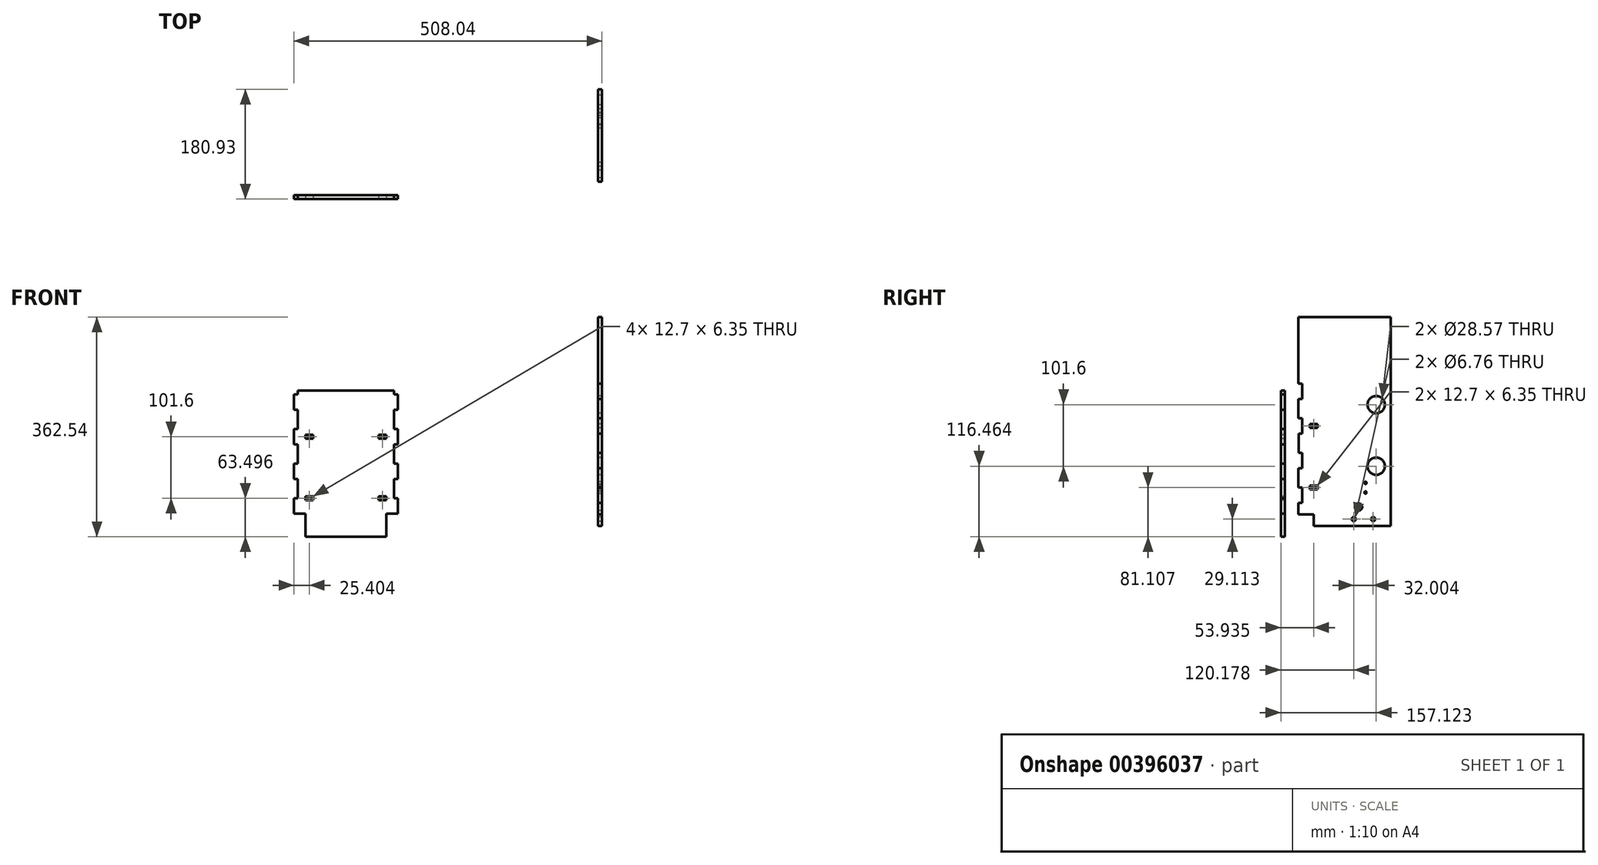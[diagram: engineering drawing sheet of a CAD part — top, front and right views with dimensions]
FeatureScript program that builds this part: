
annotation { "Feature Type Name" : "Feature", "Feature Type Description" : "" }
export const myFeature = defineFeature(function(context is Context, id is Id, definition is map)
    precondition{}
    {
        {
            var Q0;
            Q0=qCreatedBy(makeId("Front.planeOp"),FACE);
            var sketch = newSketch(context, id + "F0", { "sketchPlane" : qUnion([Q0])});
            skLineSegment(sketch, "E0.top", {"start": v(-501.69, -243.4) * mm, "end": v(-330.24, -243.4) * mm});
            skLineSegment(sketch, "E1", {"start": v(-495.34, -2.1) * mm, "end": v(-495.34, -243.4) * mm});
            skLineSegment(sketch, "E2", {"start": v(-501.69, -8.44) * mm, "end": v(-495.34, -8.44) * mm});
            skLineSegment(sketch, "E3", {"start": v(-501.69, -33.84) * mm, "end": v(-495.34, -33.84) * mm});
            skLineSegment(sketch, "E4", {"start": v(-501.69, -65.6) * mm, "end": v(-495.34, -65.6) * mm});
            skLineSegment(sketch, "E5", {"start": v(-501.69, -91) * mm, "end": v(-495.34, -91) * mm});
            skLineSegment(sketch, "E6", {"start": v(-501.69, -122.74) * mm, "end": v(-495.34, -122.74) * mm});
            skLineSegment(sketch, "E7", {"start": v(-501.69, -148.14) * mm, "end": v(-495.34, -148.14) * mm});
            skLineSegment(sketch, "E8", {"start": v(-501.69, -179.9) * mm, "end": v(-495.34, -179.9) * mm});
            skLineSegment(sketch, "E9", {"start": v(-501.69, -205.3) * mm, "end": v(-495.34, -205.3) * mm});
            skLineSegment(sketch, "E10", {"start": v(-501.69, -237.04) * mm, "end": v(-495.34, -237.04) * mm});
            skLineSegment(sketch, "E11", {"start": v(-501.69, -8.44) * mm, "end": v(-501.69, -33.84) * mm});
            skLineSegment(sketch, "E12", {"start": v(-501.69, -65.6) * mm, "end": v(-501.69, -91) * mm});
            skLineSegment(sketch, "E13", {"start": v(-501.69, -122.74) * mm, "end": v(-501.69, -148.14) * mm});
            skLineSegment(sketch, "E14", {"start": v(-501.69, -179.9) * mm, "end": v(-501.69, -205.3) * mm});
            skLineSegment(sketch, "E15", {"start": v(-501.69, -237.04) * mm, "end": v(-501.69, -243.4) * mm});
            skLineSegment(sketch, "E16", {"start": v(-336.59, -2.1) * mm, "end": v(-336.59, -243.4) * mm});
            skLineSegment(sketch, "E17", {"start": v(-336.59, -8.44) * mm, "end": v(-330.24, -8.44) * mm});
            skLineSegment(sketch, "E18", {"start": v(-336.59, -33.84) * mm, "end": v(-330.24, -33.84) * mm});
            skLineSegment(sketch, "E19", {"start": v(-336.59, -65.6) * mm, "end": v(-330.24, -65.6) * mm});
            skLineSegment(sketch, "E20", {"start": v(-336.59, -91) * mm, "end": v(-330.24, -91) * mm});
            skLineSegment(sketch, "E21", {"start": v(-336.59, -122.74) * mm, "end": v(-330.24, -122.74) * mm});
            skLineSegment(sketch, "E22", {"start": v(-336.59, -148.14) * mm, "end": v(-330.24, -148.14) * mm});
            skLineSegment(sketch, "E23", {"start": v(-336.59, -179.9) * mm, "end": v(-330.24, -179.9) * mm});
            skLineSegment(sketch, "E24", {"start": v(-336.59, -205.3) * mm, "end": v(-330.24, -205.3) * mm});
            skLineSegment(sketch, "E25", {"start": v(-336.59, -237.04) * mm, "end": v(-330.24, -237.04) * mm});
            skLineSegment(sketch, "E26", {"start": v(-330.24, -8.44) * mm, "end": v(-330.24, -33.84) * mm});
            skLineSegment(sketch, "E27", {"start": v(-330.24, -65.6) * mm, "end": v(-330.24, -91) * mm});
            skLineSegment(sketch, "E28", {"start": v(-330.24, -122.74) * mm, "end": v(-330.24, -148.14) * mm});
            skLineSegment(sketch, "E29", {"start": v(-330.24, -179.9) * mm, "end": v(-330.24, -205.3) * mm});
            skLineSegment(sketch, "E30", {"start": v(-330.24, -237.04) * mm, "end": v(-330.24, -243.4) * mm});
            skLineSegment(sketch, "E31", {"start": v(-495.34, -2.1) * mm, "end": v(-336.59, -2.1) * mm});
            skSolve(sketch);
        }
        {
            var Q0;
            {var subQ5=sQuery(id+"F0.wireOp",EDGE,"E0.bottom");var subQ8=sQuery(id+"F0.wireOp",EDGE,"E1");var subQ20=makeQuery(id+"F0.imprint","INTERSECT",VERTEX,{"derivedFrom":[subQ5,subQ8]});Q0=makeQuery(id+"F0.imprint","IMPRINT",FACE,{"disambiguationData":[TD([[makeQuery(id+"F0.imprint","IMPRINT",EDGE,{"disambiguationData":[TD([[subQ20,-1.0]])],"derivedFrom":subQ5}),-1.0]])]});}
            var Q1;
            {var subQ4=sQuery(id+"F0.wireOp",EDGE,"LMsAul2w-vVBP-qz1e-n2hl-ZY3DGVZ1hmQM");Q1=makeQuery(id+"F0.imprint","IMPRINT",FACE,{"disambiguationData":[TD([[makeQuery(id+"F0.imprint","IMPRINT",EDGE,{"derivedFrom":subQ4}),1.0]])]});}
            var Q2;
            {var subQ0=sQuery(id+"F0.wireOp",EDGE,"E2");Q2=makeQuery(id+"F0.imprint","IMPRINT",FACE,{"disambiguationData":[TD([[makeQuery(id+"F0.imprint","IMPRINT",EDGE,{"derivedFrom":subQ0}),-1.0]])]});}
            var Q3;
            {var subQ0=sQuery(id+"F0.wireOp",EDGE,"E4");Q3=makeQuery(id+"F0.imprint","IMPRINT",FACE,{"disambiguationData":[TD([[makeQuery(id+"F0.imprint","IMPRINT",EDGE,{"derivedFrom":subQ0}),-1.0]])]});}
            var Q4;
            {var subQ0=sQuery(id+"F0.wireOp",EDGE,"E6");Q4=makeQuery(id+"F0.imprint","IMPRINT",FACE,{"disambiguationData":[TD([[makeQuery(id+"F0.imprint","IMPRINT",EDGE,{"derivedFrom":subQ0}),-1.0]])]});}
            var Q5;
            {var subQ0=sQuery(id+"F0.wireOp",EDGE,"E8");Q5=makeQuery(id+"F0.imprint","IMPRINT",FACE,{"disambiguationData":[TD([[makeQuery(id+"F0.imprint","IMPRINT",EDGE,{"derivedFrom":subQ0}),-1.0]])]});}
            var Q6;
            {var subQ4=sQuery(id+"F0.wireOp",EDGE,"E10");Q6=makeQuery(id+"F0.imprint","IMPRINT",FACE,{"disambiguationData":[TD([[makeQuery(id+"F0.imprint","IMPRINT",EDGE,{"derivedFrom":subQ4}),-1.0]])]});}
            var Q7;
            {var subQ4=sQuery(id+"F0.wireOp",EDGE,"E25");Q7=makeQuery(id+"F0.imprint","IMPRINT",FACE,{"disambiguationData":[TD([[makeQuery(id+"F0.imprint","IMPRINT",EDGE,{"derivedFrom":subQ4}),-1.0]])]});}
            var Q8;
            {var subQ0=sQuery(id+"F0.wireOp",EDGE,"E23");Q8=makeQuery(id+"F0.imprint","IMPRINT",FACE,{"disambiguationData":[TD([[makeQuery(id+"F0.imprint","IMPRINT",EDGE,{"derivedFrom":subQ0}),-1.0]])]});}
            var Q9;
            {var subQ0=sQuery(id+"F0.wireOp",EDGE,"E21");Q9=makeQuery(id+"F0.imprint","IMPRINT",FACE,{"disambiguationData":[TD([[makeQuery(id+"F0.imprint","IMPRINT",EDGE,{"derivedFrom":subQ0}),-1.0]])]});}
            var Q10;
            {var subQ0=sQuery(id+"F0.wireOp",EDGE,"E19");Q10=makeQuery(id+"F0.imprint","IMPRINT",FACE,{"disambiguationData":[TD([[makeQuery(id+"F0.imprint","IMPRINT",EDGE,{"derivedFrom":subQ0}),-1.0]])]});}
            var Q11;
            {var subQ0=sQuery(id+"F0.wireOp",EDGE,"E17");Q11=makeQuery(id+"F0.imprint","IMPRINT",FACE,{"disambiguationData":[TD([[makeQuery(id+"F0.imprint","IMPRINT",EDGE,{"derivedFrom":subQ0}),-1.0]])]});}
            var Q12;
            {var subQ4=sQuery(id+"F0.wireOp",EDGE,"Q2wxjBHx-EqrT-55AE-FTu7-pREpD65ahsZC");Q12=makeQuery(id+"F0.imprint","IMPRINT",FACE,{"disambiguationData":[TD([[makeQuery(id+"F0.imprint","IMPRINT",EDGE,{"derivedFrom":subQ4}),1.0]])]});}
            var Q13;
            {var subQ12=sQuery(id+"F0.wireOp",EDGE,"E31");Q13=makeQuery(id+"F0.imprint","IMPRINT",FACE,{"disambiguationData":[TD([[makeQuery(id+"F0.imprint","IMPRINT",EDGE,{"derivedFrom":subQ12}),-1.0]])]});}
            extrude(context, id + "F1", {"entities" : qUnion([Q0, Q1, Q2, Q3, Q4, Q5, Q6, Q7, Q8, Q9, Q10, Q11, Q12, Q13]), "depth" : 6.35 * mm});
        }
        {
            var Q0;
            Q0=qCreatedBy(makeId("Right.planeOp"),FACE);
            var sketch = newSketch(context, id + "F2", { "sketchPlane" : qUnion([Q0])});
            skLineSegment(sketch, "E32", {"start": v(28.53, -16.23) * mm, "end": v(22.18, -16.23) * mm});
            skLineSegment(sketch, "E33", {"start": v(28.53, -130.53) * mm, "end": v(22.18, -130.53) * mm});
            skLineSegment(sketch, "E34", {"start": v(28.53, -162.28) * mm, "end": v(22.18, -162.28) * mm});
            skLineSegment(sketch, "E35", {"start": v(28.53, -187.68) * mm, "end": v(22.18, -187.68) * mm});
            skLineSegment(sketch, "E36", {"start": v(28.53, -225.78) * mm, "end": v(22.18, -225.78) * mm});
            skLineSegment(sketch, "E37", {"start": v(28.53, -73.38) * mm, "end": v(22.8, -73.38) * mm});
            skLineSegment(sketch, "E38", {"start": v(28.53, -105.13) * mm, "end": v(22.8, -105.13) * mm});
            skLineSegment(sketch, "E39", {"start": v(22.8, -73.38) * mm, "end": v(22.8, -105.13) * mm});
            skLineSegment(sketch, "E40", {"start": v(22.18, -16.23) * mm, "end": v(22.18, -47.98) * mm});
            skLineSegment(sketch, "E41", {"start": v(22.18, -130.53) * mm, "end": v(22.18, -162.28) * mm});
            skLineSegment(sketch, "E42", {"start": v(22.18, -187.68) * mm, "end": v(22.18, -225.78) * mm});
            skLineSegment(sketch, "E43", {"start": v(174.58, -251.18) * mm, "end": v(28.53, -251.18) * mm});
            skLineSegment(sketch, "E44", {"start": v(22.18, 119.15) * mm, "end": v(174.58, 119.15) * mm});
            skLineSegment(sketch, "E45", {"start": v(174.58, 119.15) * mm, "end": v(174.58, -251.18) * mm});
            skLineSegment(sketch, "E46", {"start": v(28.53, -251.18) * mm, "end": v(28.53, 119.15) * mm});
            skLineSegment(sketch, "E47", {"start": v(22.18, -47.98) * mm, "end": v(28.53, -47.98) * mm});
            skLineSegment(sketch, "E48", {"start": v(28.53, 15.52) * mm, "end": v(22.18, 15.52) * mm});
            skLineSegment(sketch, "E49", {"start": v(22.18, 15.52) * mm, "end": v(22.18, 9.17) * mm});
            skLineSegment(sketch, "E50", {"start": v(22.18, 9.17) * mm, "end": v(28.53, 9.17) * mm});
            skLineSegment(sketch, "E51", {"start": v(22.18, 119.15) * mm, "end": v(22.18, 15.52) * mm});
            skLineSegment(sketch, "E52", {"start": v(28.53, -225.78) * mm, "end": v(174.58, -225.78) * mm});
            skLineSegment(sketch, "E53", {"start": v(22.18, -206.73) * mm, "end": v(47.58, -206.73) * mm});
            skLineSegment(sketch, "E54", {"start": v(47.58, -206.73) * mm, "end": v(47.58, -225.78) * mm});
            skSolve(sketch);
        }
        {
            var Q0;
            {var subQ14=sQuery(id+"F2.wireOp",EDGE,"i33fb0zR-01mT-Uh86-wEM1-dtgX8HlX7Fyt");Q0=makeQuery(id+"F2.imprint","IMPRINT",FACE,{"disambiguationData":[TD([[makeQuery(id+"F2.imprint","IMPRINT",EDGE,{"derivedFrom":subQ14}),1.0]])]});}
            var Q1;
            {var subQ4=sQuery(id+"F2.wireOp",EDGE,"rhUE6cCd-mflr-hycs-3UUx-SssaEqSjHUIw");Q1=makeQuery(id+"F2.imprint","IMPRINT",FACE,{"disambiguationData":[TD([[makeQuery(id+"F2.imprint","IMPRINT",EDGE,{"derivedFrom":subQ4}),-1.0]])]});}
            var Q2;
            {var subQ0=sQuery(id+"F2.wireOp",EDGE,"1oS58uJ2-hXIY-gExO-wKBo-R9qEpw5Eswbh");Q2=makeQuery(id+"F2.imprint","IMPRINT",FACE,{"disambiguationData":[TD([[makeQuery(id+"F2.imprint","IMPRINT",EDGE,{"derivedFrom":subQ0}),1.0]])]});}
            var Q3;
            {var subQ0=sQuery(id+"F2.wireOp",EDGE,"HLNgD7Xm-XkV7-PYZ1-Vyr9-8PbT4umlXNnn");Q3=makeQuery(id+"F2.imprint","IMPRINT",FACE,{"disambiguationData":[TD([[makeQuery(id+"F2.imprint","IMPRINT",EDGE,{"derivedFrom":subQ0}),1.0]])]});}
            var Q4;
            {var subQ0=sQuery(id+"F2.wireOp",EDGE,"S2SFkNX2-MHnE-1LtQ-Wrl6-HN21gxM6cwIg.top");Q4=makeQuery(id+"F2.imprint","IMPRINT",FACE,{"disambiguationData":[TD([[makeQuery(id+"F2.imprint","IMPRINT",EDGE,{"derivedFrom":subQ0}),1.0]])]});}
            var Q5;
            {var subQ0=sQuery(id+"F2.wireOp",EDGE,"nHbaO1BD-I0WF-YKfL-4D9o-AtkHzTHVU68h");Q5=makeQuery(id+"F2.imprint","IMPRINT",FACE,{"disambiguationData":[TD([[makeQuery(id+"F2.imprint","IMPRINT",EDGE,{"derivedFrom":subQ0}),1.0]])]});}
            var Q6;
            {var subQ0=sQuery(id+"F2.wireOp",EDGE,"e9KHasA0-oYsS-l2PR-DguL-FNIX4GsAtZwv");Q6=makeQuery(id+"F2.imprint","IMPRINT",FACE,{"disambiguationData":[TD([[makeQuery(id+"F2.imprint","IMPRINT",EDGE,{"derivedFrom":subQ0}),1.0]])]});}
            var Q7;
            {var subQ0=sQuery(id+"F2.wireOp",EDGE,"E37");Q7=makeQuery(id+"F2.imprint","IMPRINT",FACE,{"disambiguationData":[TD([[makeQuery(id+"F2.imprint","IMPRINT",EDGE,{"derivedFrom":subQ0}),1.0]])]});}
            var Q8;
            {var subQ0=sQuery(id+"F2.wireOp",EDGE,"E32");Q8=makeQuery(id+"F2.imprint","IMPRINT",FACE,{"disambiguationData":[TD([[makeQuery(id+"F2.imprint","IMPRINT",EDGE,{"derivedFrom":subQ0}),1.0]])]});}
            var Q9;
            {var subQ0=sQuery(id+"F2.wireOp",EDGE,"gp76ZxvM-iRQH-n3sY-OGDD-mYjBX4D9k2O5");Q9=makeQuery(id+"F2.imprint","IMPRINT",FACE,{"disambiguationData":[TD([[makeQuery(id+"F2.imprint","IMPRINT",EDGE,{"derivedFrom":subQ0}),1.0]])]});}
            var Q10;
            {var subQ0=sQuery(id+"F2.wireOp",EDGE,"E33");Q10=makeQuery(id+"F2.imprint","IMPRINT",FACE,{"disambiguationData":[TD([[makeQuery(id+"F2.imprint","IMPRINT",EDGE,{"derivedFrom":subQ0}),1.0]])]});}
            var Q11;
            {var subQ0=sQuery(id+"F2.wireOp",EDGE,"E35");Q11=makeQuery(id+"F2.imprint","IMPRINT",FACE,{"disambiguationData":[TD([[makeQuery(id+"F2.imprint","IMPRINT",EDGE,{"derivedFrom":subQ0}),1.0]])]});}
            var Q12;
            {var subQ4=sQuery(id+"F2.wireOp",EDGE,"E48");Q12=makeQuery(id+"F2.imprint","IMPRINT",FACE,{"disambiguationData":[TD([[makeQuery(id+"F2.imprint","IMPRINT",EDGE,{"derivedFrom":subQ4}),-1.0]])]});}
            var Q13;
            {var subQ0=sQuery(id+"F2.wireOp",EDGE,"E48");Q13=makeQuery(id+"F2.imprint","IMPRINT",FACE,{"disambiguationData":[TD([[makeQuery(id+"F2.imprint","IMPRINT",EDGE,{"derivedFrom":subQ0}),1.0]])]});}
            var Q14;
            {var subQ6=sQuery(id+"F2.wireOp",EDGE,"E54");Q14=makeQuery(id+"F2.imprint","IMPRINT",FACE,{"disambiguationData":[TD([[makeQuery(id+"F2.imprint","IMPRINT",EDGE,{"derivedFrom":subQ6}),1.0]])]});}
            extrude(context, id + "F3", {"entities" : qUnion([Q0, Q1, Q2, Q3, Q4, Q5, Q6, Q7, Q8, Q9, Q10, Q11, Q12, Q13, Q14]), "depth" : 6.35 * mm});
        }
        {
            var Q0;
            Q0=makeQuery(id+"F3.opExtrude","CAP_FACE",FACE,{"disambiguationData":[OSD([sQuery(id+"F2.wireOp",EDGE,"s0DKLVIk-yI4o-mbJo-Qtl3-NwG1ndSy3CrT"),sQuery(id+"F2.wireOp",EDGE,"E32"),sQuery(id+"F2.wireOp",EDGE,"bUhOaF83-sfzh-5jzX-XBu8-1UuN6AYuXBg6"),sQuery(id+"F2.wireOp",EDGE,"gp76ZxvM-iRQH-n3sY-OGDD-mYjBX4D9k2O5"),sQuery(id+"F2.wireOp",EDGE,"5Qirrqq4-OgZc-HNT0-THzN-mm1dnDsTKt5a"),sQuery(id+"F2.wireOp",EDGE,"E33"),sQuery(id+"F2.wireOp",EDGE,"E34"),sQuery(id+"F2.wireOp",EDGE,"E35"),sQuery(id+"F2.wireOp",EDGE,"E36"),sQuery(id+"F2.wireOp",EDGE,"rhUE6cCd-mflr-hycs-3UUx-SssaEqSjHUIw"),sQuery(id+"F2.wireOp",EDGE,"E37"),sQuery(id+"F2.wireOp",EDGE,"E38"),sQuery(id+"F2.wireOp",EDGE,"XDC90Sgm-SAT4-zVe1-7gUu-QymedyxHn4AY"),sQuery(id+"F2.wireOp",EDGE,"E39"),sQuery(id+"F2.wireOp",EDGE,"E40"),sQuery(id+"F2.wireOp",EDGE,"Gb2Q8Irj-KXKR-EalS-J060-aK0soJo5RwYU"),sQuery(id+"F2.wireOp",EDGE,"E41"),sQuery(id+"F2.wireOp",EDGE,"E42"),sQuery(id+"F2.wireOp",EDGE,"E43"),sQuery(id+"F2.wireOp",EDGE,"E44"),sQuery(id+"F2.wireOp",EDGE,"E45")])],"isStart":true});
            var sketch = newSketch(context, id + "F4", { "sketchPlane" : qUnion([Q0])});
            skCircle(sketch, "E55", {"center": v(-150.77, -126.93) * mm, "radius": 14.29 * mm});
            skCircle(sketch, "E56", {"center": v(-150.77, -25.33) * mm, "radius": 14.29 * mm});
            skSolve(sketch);
        }
        {
            var Q0;
            Q0=makeQuery(id+"F4.imprint","IMPRINT",FACE,{"disambiguationData":[TD([[makeQuery(id+"F4.imprint","IMPRINT",EDGE,{"derivedFrom":sQuery(id+"F4.wireOp",EDGE,"E56")}),1.0]])]});
            var Q1;
            Q1=makeQuery(id+"F4.imprint","IMPRINT",FACE,{"disambiguationData":[TD([[makeQuery(id+"F4.imprint","IMPRINT",EDGE,{"derivedFrom":sQuery(id+"F4.wireOp",EDGE,"E55")}),1.0]])]});
            extrude(context, id + "F5", {"entities" : qUnion([Q0, Q1]), "operationType" : NewBodyOperationType.REMOVE, "oppositeDirection" : true, "depth" : 6.35 * mm});
        }
        {
            var Q0;
            Q0=makeQuery(id+"F3.opExtrude","CAP_FACE",FACE,{"disambiguationData":[OSD([sQuery(id+"F2.wireOp",EDGE,"s0DKLVIk-yI4o-mbJo-Qtl3-NwG1ndSy3CrT"),sQuery(id+"F2.wireOp",EDGE,"E32"),sQuery(id+"F2.wireOp",EDGE,"bUhOaF83-sfzh-5jzX-XBu8-1UuN6AYuXBg6"),sQuery(id+"F2.wireOp",EDGE,"gp76ZxvM-iRQH-n3sY-OGDD-mYjBX4D9k2O5"),sQuery(id+"F2.wireOp",EDGE,"5Qirrqq4-OgZc-HNT0-THzN-mm1dnDsTKt5a"),sQuery(id+"F2.wireOp",EDGE,"E33"),sQuery(id+"F2.wireOp",EDGE,"E34"),sQuery(id+"F2.wireOp",EDGE,"E35"),sQuery(id+"F2.wireOp",EDGE,"E36"),sQuery(id+"F2.wireOp",EDGE,"rhUE6cCd-mflr-hycs-3UUx-SssaEqSjHUIw"),sQuery(id+"F2.wireOp",EDGE,"E37"),sQuery(id+"F2.wireOp",EDGE,"E38"),sQuery(id+"F2.wireOp",EDGE,"XDC90Sgm-SAT4-zVe1-7gUu-QymedyxHn4AY"),sQuery(id+"F2.wireOp",EDGE,"E39"),sQuery(id+"F2.wireOp",EDGE,"E40"),sQuery(id+"F2.wireOp",EDGE,"Gb2Q8Irj-KXKR-EalS-J060-aK0soJo5RwYU"),sQuery(id+"F2.wireOp",EDGE,"E41"),sQuery(id+"F2.wireOp",EDGE,"E42"),sQuery(id+"F2.wireOp",EDGE,"E43"),sQuery(id+"F2.wireOp",EDGE,"E44"),sQuery(id+"F2.wireOp",EDGE,"E45")])],"isStart":true});
            var sketch = newSketch(context, id + "F6", { "sketchPlane" : qUnion([Q0])});
            skLineSegment(sketch, "E57.bottom", {"start": v(-53.93, -159.1) * mm, "end": v(-41.23, -159.1) * mm});
            skLineSegment(sketch, "E57.top", {"start": v(-53.93, -165.46) * mm, "end": v(-41.23, -165.46) * mm});
            skLineSegment(sketch, "E57.left", {"start": v(-53.93, -159.1) * mm, "end": v(-53.93, -165.46) * mm});
            skLineSegment(sketch, "E57.right", {"start": v(-41.23, -159.1) * mm, "end": v(-41.23, -165.46) * mm});
            skLineSegment(sketch, "E58.bottom", {"start": v(-53.93, -57.5) * mm, "end": v(-41.23, -57.5) * mm});
            skLineSegment(sketch, "E58.top", {"start": v(-53.93, -63.86) * mm, "end": v(-41.23, -63.86) * mm});
            skLineSegment(sketch, "E58.left", {"start": v(-53.93, -57.5) * mm, "end": v(-53.93, -63.86) * mm});
            skLineSegment(sketch, "E58.right", {"start": v(-41.23, -57.5) * mm, "end": v(-41.23, -63.86) * mm});
            skSolve(sketch);
        }
        {
            var Q0;
            Q0=makeQuery(id+"F6.imprint","IMPRINT",FACE,{"disambiguationData":[TD([[makeQuery(id+"F6.imprint","IMPRINT",EDGE,{"derivedFrom":sQuery(id+"F6.wireOp",EDGE,"zmTBmbvl-Oux8-fxHu-hAO5-6Uis3kAJMw4c.bottom")}),-1.0]])]});
            var Q1;
            Q1=makeQuery(id+"F6.imprint","IMPRINT",FACE,{"disambiguationData":[TD([[makeQuery(id+"F6.imprint","IMPRINT",EDGE,{"derivedFrom":sQuery(id+"F6.wireOp",EDGE,"E58.bottom")}),-1.0]])]});
            var Q2;
            Q2=makeQuery(id+"F6.imprint","IMPRINT",FACE,{"disambiguationData":[TD([[makeQuery(id+"F6.imprint","IMPRINT",EDGE,{"derivedFrom":sQuery(id+"F6.wireOp",EDGE,"E57.bottom")}),-1.0]])]});
            extrude(context, id + "F7", {"entities" : qUnion([Q0, Q1, Q2]), "operationType" : NewBodyOperationType.REMOVE, "oppositeDirection" : true, "depth" : 6.35 * mm});
        }
        {
            var Q0;
            Q0=makeQuery(id+"F1.opExtrude","CAP_FACE",FACE,{"disambiguationData":[OSD([sQuery(id+"F0.wireOp",EDGE,"E0.bottom"),sQuery(id+"F0.wireOp",EDGE,"E0.top"),sQuery(id+"F0.wireOp",EDGE,"E1"),sQuery(id+"F0.wireOp",EDGE,"LMsAul2w-vVBP-qz1e-n2hl-ZY3DGVZ1hmQM"),sQuery(id+"F0.wireOp",EDGE,"E2"),sQuery(id+"F0.wireOp",EDGE,"E3"),sQuery(id+"F0.wireOp",EDGE,"E4"),sQuery(id+"F0.wireOp",EDGE,"E5"),sQuery(id+"F0.wireOp",EDGE,"E6"),sQuery(id+"F0.wireOp",EDGE,"E7"),sQuery(id+"F0.wireOp",EDGE,"E8"),sQuery(id+"F0.wireOp",EDGE,"E9"),sQuery(id+"F0.wireOp",EDGE,"E10"),sQuery(id+"F0.wireOp",EDGE,"fckjmxOd-PKS0-K6HS-jWLe-0Rm2YWeLxNei"),sQuery(id+"F0.wireOp",EDGE,"E11"),sQuery(id+"F0.wireOp",EDGE,"E12"),sQuery(id+"F0.wireOp",EDGE,"E13"),sQuery(id+"F0.wireOp",EDGE,"E14"),sQuery(id+"F0.wireOp",EDGE,"E15"),sQuery(id+"F0.wireOp",EDGE,"E16"),sQuery(id+"F0.wireOp",EDGE,"Q2wxjBHx-EqrT-55AE-FTu7-pREpD65ahsZC"),sQuery(id+"F0.wireOp",EDGE,"E17"),sQuery(id+"F0.wireOp",EDGE,"E18"),sQuery(id+"F0.wireOp",EDGE,"E19"),sQuery(id+"F0.wireOp",EDGE,"E20"),sQuery(id+"F0.wireOp",EDGE,"E21"),sQuery(id+"F0.wireOp",EDGE,"E22"),sQuery(id+"F0.wireOp",EDGE,"E23"),sQuery(id+"F0.wireOp",EDGE,"E24"),sQuery(id+"F0.wireOp",EDGE,"E25"),sQuery(id+"F0.wireOp",EDGE,"p0LhYthy-u7VA-cxhh-v3hJ-NGUNxxqC1vMh"),sQuery(id+"F0.wireOp",EDGE,"E26"),sQuery(id+"F0.wireOp",EDGE,"E27"),sQuery(id+"F0.wireOp",EDGE,"E28"),sQuery(id+"F0.wireOp",EDGE,"E29"),sQuery(id+"F0.wireOp",EDGE,"E30")])],"isStart":false});
            var sketch = newSketch(context, id + "F8", { "sketchPlane" : qUnion([Q0])});
            skLineSegment(sketch, "E59.bottom", {"start": v(-482.64, -75.12) * mm, "end": v(-469.94, -75.12) * mm});
            skLineSegment(sketch, "E59.top", {"start": v(-482.64, -81.47) * mm, "end": v(-469.94, -81.47) * mm});
            skLineSegment(sketch, "E59.left", {"start": v(-482.64, -75.12) * mm, "end": v(-482.64, -81.47) * mm});
            skLineSegment(sketch, "E59.right", {"start": v(-469.94, -75.12) * mm, "end": v(-469.94, -81.47) * mm});
            skLineSegment(sketch, "E60.bottom", {"start": v(-482.64, -176.72) * mm, "end": v(-469.94, -176.72) * mm});
            skLineSegment(sketch, "E60.top", {"start": v(-482.64, -183.07) * mm, "end": v(-469.94, -183.07) * mm});
            skLineSegment(sketch, "E60.left", {"start": v(-482.64, -176.72) * mm, "end": v(-482.64, -183.07) * mm});
            skLineSegment(sketch, "E60.right", {"start": v(-469.94, -176.72) * mm, "end": v(-469.94, -183.07) * mm});
            skLineSegment(sketch, "E61.bottom", {"start": v(-361.99, -75.12) * mm, "end": v(-349.29, -75.12) * mm});
            skLineSegment(sketch, "E61.top", {"start": v(-361.99, -81.47) * mm, "end": v(-349.29, -81.47) * mm});
            skLineSegment(sketch, "E61.left", {"start": v(-361.99, -75.12) * mm, "end": v(-361.99, -81.47) * mm});
            skLineSegment(sketch, "E61.right", {"start": v(-349.29, -75.12) * mm, "end": v(-349.29, -81.47) * mm});
            skLineSegment(sketch, "E62.bottom", {"start": v(-361.99, -176.72) * mm, "end": v(-349.29, -176.72) * mm});
            skLineSegment(sketch, "E62.top", {"start": v(-361.99, -183.07) * mm, "end": v(-349.29, -183.07) * mm});
            skLineSegment(sketch, "E62.left", {"start": v(-361.99, -176.72) * mm, "end": v(-361.99, -183.07) * mm});
            skLineSegment(sketch, "E62.right", {"start": v(-349.29, -176.72) * mm, "end": v(-349.29, -183.07) * mm});
            skSolve(sketch);
        }
        {
            var Q0;
            Q0=qSketchRegion(id+"F8",true);
            extrude(context, id + "F9", {"entities" : qUnion([Q0]), "operationType" : NewBodyOperationType.REMOVE, "oppositeDirection" : true, "depth" : 6.35 * mm});
        }
        {
            var Q0;
            Q0=makeQuery(id+"F1.opExtrude","CAP_FACE",FACE,{"disambiguationData":[OSD([sQuery(id+"F0.wireOp",EDGE,"E0.top"),sQuery(id+"F0.wireOp",EDGE,"E1"),sQuery(id+"F0.wireOp",EDGE,"E2"),sQuery(id+"F0.wireOp",EDGE,"E3"),sQuery(id+"F0.wireOp",EDGE,"E4"),sQuery(id+"F0.wireOp",EDGE,"E5"),sQuery(id+"F0.wireOp",EDGE,"E6"),sQuery(id+"F0.wireOp",EDGE,"E7"),sQuery(id+"F0.wireOp",EDGE,"E8"),sQuery(id+"F0.wireOp",EDGE,"E9"),sQuery(id+"F0.wireOp",EDGE,"E10"),sQuery(id+"F0.wireOp",EDGE,"E11"),sQuery(id+"F0.wireOp",EDGE,"E12"),sQuery(id+"F0.wireOp",EDGE,"E13"),sQuery(id+"F0.wireOp",EDGE,"E14"),sQuery(id+"F0.wireOp",EDGE,"E15"),sQuery(id+"F0.wireOp",EDGE,"E16"),sQuery(id+"F0.wireOp",EDGE,"E17"),sQuery(id+"F0.wireOp",EDGE,"E18"),sQuery(id+"F0.wireOp",EDGE,"E19"),sQuery(id+"F0.wireOp",EDGE,"E20"),sQuery(id+"F0.wireOp",EDGE,"E21"),sQuery(id+"F0.wireOp",EDGE,"E22"),sQuery(id+"F0.wireOp",EDGE,"E23"),sQuery(id+"F0.wireOp",EDGE,"E24"),sQuery(id+"F0.wireOp",EDGE,"E25"),sQuery(id+"F0.wireOp",EDGE,"E26"),sQuery(id+"F0.wireOp",EDGE,"E27"),sQuery(id+"F0.wireOp",EDGE,"E28"),sQuery(id+"F0.wireOp",EDGE,"E29"),sQuery(id+"F0.wireOp",EDGE,"E30"),sQuery(id+"F0.wireOp",EDGE,"E31")])],"isStart":false});
            var sketch = newSketch(context, id + "F10", { "sketchPlane" : qUnion([Q0])});
            skLineSegment(sketch, "E63", {"start": v(-482.64, -243.4) * mm, "end": v(-482.64, -205.3) * mm});
            skLineSegment(sketch, "E64", {"start": v(-482.64, -205.3) * mm, "end": v(-501.69, -205.3) * mm});
            skLineSegment(sketch, "E65", {"start": v(-501.69, -205.3) * mm, "end": v(-501.69, -243.4) * mm});
            skLineSegment(sketch, "E66.bottom", {"start": v(-330.24, -243.4) * mm, "end": v(-349.29, -243.4) * mm});
            skLineSegment(sketch, "E66.top", {"start": v(-330.24, -205.3) * mm, "end": v(-349.29, -205.3) * mm});
            skLineSegment(sketch, "E66.left", {"start": v(-330.24, -243.4) * mm, "end": v(-330.24, -205.3) * mm});
            skLineSegment(sketch, "E66.right", {"start": v(-349.29, -243.4) * mm, "end": v(-349.29, -205.3) * mm});
            skSolve(sketch);
        }
        {
            var Q0;
            {var subQ3=sQuery(id+"F10.wireOp",EDGE,"E63");Q0=makeQuery(id+"F10.imprint","IMPRINT",FACE,{"disambiguationData":[TD([[makeQuery(id+"F10.imprint","IMPRINT",EDGE,{"derivedFrom":subQ3}),1.0]])]});}
            var Q1;
            {var subQ2=sQuery(id+"F10.wireOp",EDGE,"E66.bottom");Q1=makeQuery(id+"F10.imprint","IMPRINT",FACE,{"disambiguationData":[TD([[makeQuery(id+"F10.imprint","IMPRINT",EDGE,{"derivedFrom":subQ2}),1.0]])]});}
            extrude(context, id + "F11", {"entities" : qUnion([Q0, Q1]), "operationType" : NewBodyOperationType.REMOVE, "oppositeDirection" : true, "depth" : 6.35 * mm});
        }
        {
            var Q0;
            Q0=makeQuery(id+"F3.opExtrude","CAP_FACE",FACE,{"disambiguationData":[OSD([sQuery(id+"F2.wireOp",EDGE,"E32"),sQuery(id+"F2.wireOp",EDGE,"E33"),sQuery(id+"F2.wireOp",EDGE,"E34"),sQuery(id+"F2.wireOp",EDGE,"E35"),sQuery(id+"F2.wireOp",EDGE,"E37"),sQuery(id+"F2.wireOp",EDGE,"E38"),sQuery(id+"F2.wireOp",EDGE,"E39"),sQuery(id+"F2.wireOp",EDGE,"E40"),sQuery(id+"F2.wireOp",EDGE,"E41"),sQuery(id+"F2.wireOp",EDGE,"E42"),sQuery(id+"F2.wireOp",EDGE,"E44"),sQuery(id+"F2.wireOp",EDGE,"E45"),sQuery(id+"F2.wireOp",EDGE,"E46"),sQuery(id+"F2.wireOp",EDGE,"E47"),sQuery(id+"F2.wireOp",EDGE,"E49"),sQuery(id+"F2.wireOp",EDGE,"E50"),sQuery(id+"F2.wireOp",EDGE,"E51"),sQuery(id+"F2.wireOp",EDGE,"E52"),sQuery(id+"F2.wireOp",EDGE,"E53"),sQuery(id+"F2.wireOp",EDGE,"E54")])],"isStart":true});
            var sketch = newSketch(context, id + "F12", { "sketchPlane" : qUnion([Q0])});
            skCircle(sketch, "E67", {"center": v(-121.63, -194.31) * mm, "radius": 6 * mm});
            skSolve(sketch);
        }
        {
            var Q0;
            Q0=makeQuery(id+"F12.imprint","IMPRINT",FACE,{"disambiguationData":[TD([[makeQuery(id+"F12.imprint","IMPRINT",EDGE,{"derivedFrom":sQuery(id+"F12.wireOp",EDGE,"E67")}),1.0]])]});
            var Q1;
            Q1=sQuery(id+"F12.wireOp",EDGE,"E67");
            extrude(context, id + "F13", {"entities" : qUnion([Q0]), "operationType" : NewBodyOperationType.REMOVE, "surfaceEntities" : qUnion([Q1]), "oppositeDirection" : true, "depth" : 25.4 * mm});
        }
        {
            var Q0;
            Q0=makeQuery(id+"F3.opExtrude","CAP_FACE",FACE,{"disambiguationData":[OSD([sQuery(id+"F2.wireOp",EDGE,"E32"),sQuery(id+"F2.wireOp",EDGE,"E33"),sQuery(id+"F2.wireOp",EDGE,"E34"),sQuery(id+"F2.wireOp",EDGE,"E35"),sQuery(id+"F2.wireOp",EDGE,"E37"),sQuery(id+"F2.wireOp",EDGE,"E38"),sQuery(id+"F2.wireOp",EDGE,"E39"),sQuery(id+"F2.wireOp",EDGE,"E40"),sQuery(id+"F2.wireOp",EDGE,"E41"),sQuery(id+"F2.wireOp",EDGE,"E42"),sQuery(id+"F2.wireOp",EDGE,"E44"),sQuery(id+"F2.wireOp",EDGE,"E45"),sQuery(id+"F2.wireOp",EDGE,"E46"),sQuery(id+"F2.wireOp",EDGE,"E47"),sQuery(id+"F2.wireOp",EDGE,"E49"),sQuery(id+"F2.wireOp",EDGE,"E50"),sQuery(id+"F2.wireOp",EDGE,"E51"),sQuery(id+"F2.wireOp",EDGE,"E52"),sQuery(id+"F2.wireOp",EDGE,"E53"),sQuery(id+"F2.wireOp",EDGE,"E54")])],"isStart":true});
            var sketch = newSketch(context, id + "F14", { "sketchPlane" : qUnion([Q0])});
            skCircle(sketch, "E68", {"center": v(-145.83, -214.28) * mm, "radius": 3.38 * mm});
            skCircle(sketch, "E69", {"center": v(-113.83, -214.28) * mm, "radius": 3.38 * mm});
            skCircle(sketch, "E70", {"center": v(-133.2, -154.38) * mm, "radius": 1.9 * mm});
            skCircle(sketch, "E71", {"center": v(-133.2, -170.39) * mm, "radius": 1.9 * mm});
            skSolve(sketch);
        }
        {
            var Q0;
            Q0=makeQuery(id+"F14.imprint","IMPRINT",FACE,{"disambiguationData":[TD([[makeQuery(id+"F14.imprint","IMPRINT",EDGE,{"derivedFrom":sQuery(id+"F14.wireOp",EDGE,"E68")}),1.0]])]});
            var Q1;
            Q1=makeQuery(id+"F14.imprint","IMPRINT",FACE,{"disambiguationData":[TD([[makeQuery(id+"F14.imprint","IMPRINT",EDGE,{"derivedFrom":sQuery(id+"F14.wireOp",EDGE,"E69")}),1.0]])]});
            var Q2;
            Q2=makeQuery(id+"F14.imprint","IMPRINT",FACE,{"disambiguationData":[TD([[makeQuery(id+"F14.imprint","IMPRINT",EDGE,{"derivedFrom":sQuery(id+"F14.wireOp",EDGE,"E71")}),1.0]])]});
            var Q3;
            Q3=makeQuery(id+"F14.imprint","IMPRINT",FACE,{"disambiguationData":[TD([[makeQuery(id+"F14.imprint","IMPRINT",EDGE,{"derivedFrom":sQuery(id+"F14.wireOp",EDGE,"E70")}),1.0]])]});
            extrude(context, id + "F15", {"entities" : qUnion([Q0, Q1, Q2, Q3]), "operationType" : NewBodyOperationType.REMOVE, "oppositeDirection" : true, "depth" : 6.35 * mm});
        }
    });
